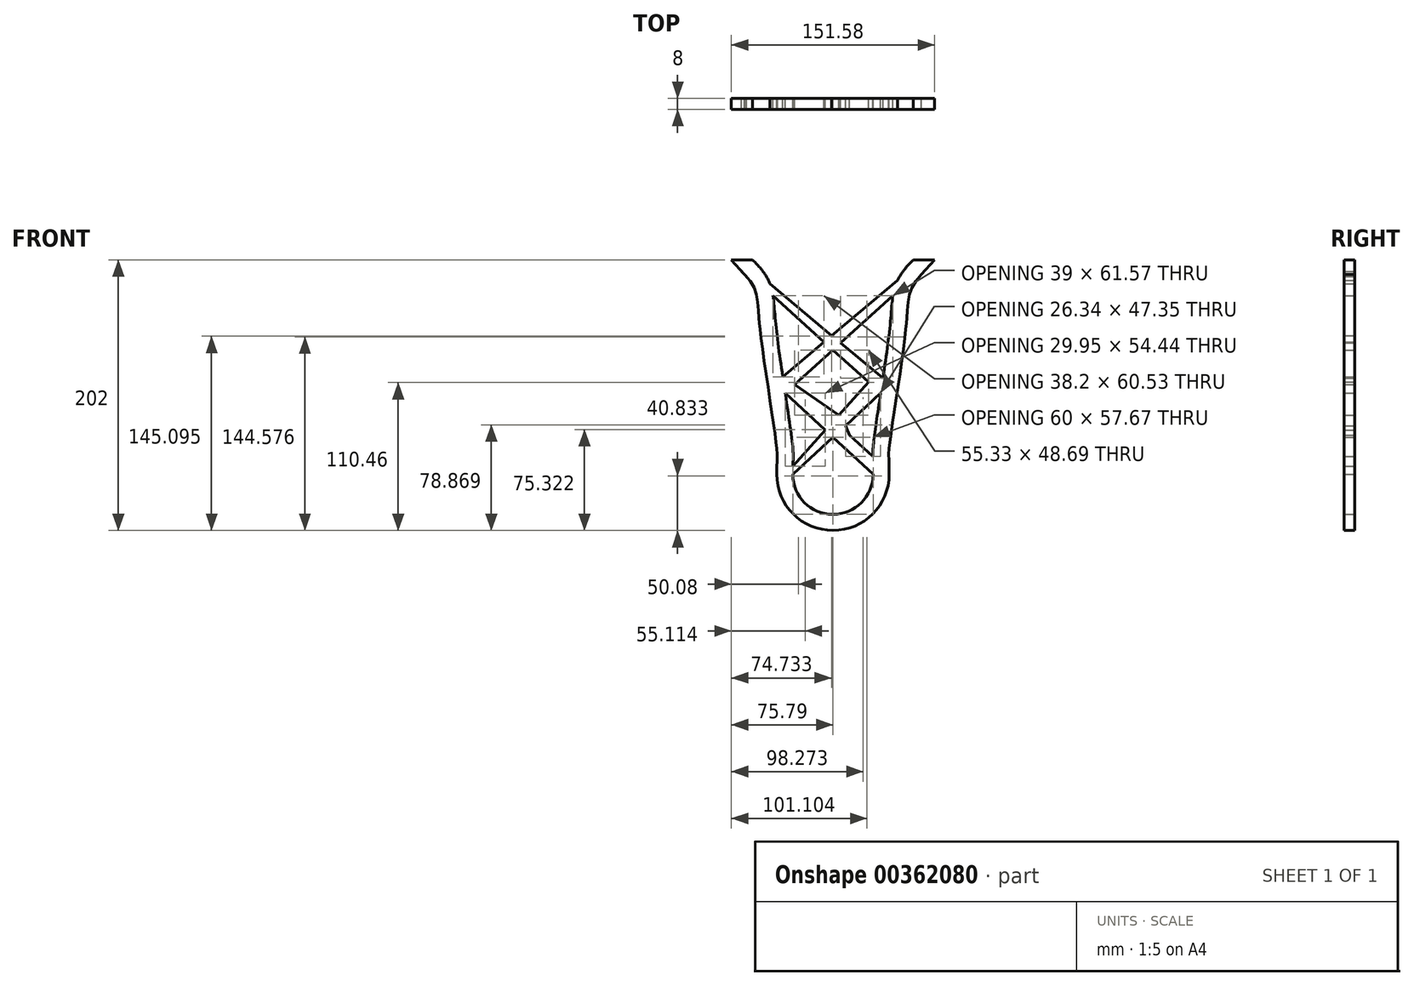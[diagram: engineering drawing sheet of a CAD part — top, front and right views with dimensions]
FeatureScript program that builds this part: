
annotation { "Feature Type Name" : "Feature", "Feature Type Description" : "" }
export const myFeature = defineFeature(function(context is Context, id is Id, definition is map)
    precondition{}
    {
        {
            var Q0;
            Q0=qCreatedBy(makeId("Front.planeOp"),FACE);
            var sketch = newSketch(context, id + "F0", { "sketchPlane" : qUnion([Q0])});
            skArc(sketch, "E0", {"start": v(-30, 0) * mm, "mid": v(0, -30) * mm, "end": v(30, 0) * mm});
            skLineSegment(sketch, "E1", {"start": v(30, 0) * mm, "end": v(0, 0) * mm, "construction": true});
            skLineSegment(sketch, "E2", {"start": v(-30, 0) * mm, "end": v(0, 0) * mm, "construction": true});
            skFitSpline(sketch, "E3", {"points": [v(30, 0) * mm, v(30, 20) * mm, v(43, 115) * mm, v(60, 160) * mm], "startDerivative": vector(0, 145.41) * mm, "endDerivative": vector(149.4, 141.79) * mm});
            skLineSegment(sketch, "E4", {"start": v(0, 0) * mm, "end": v(0, 155.66) * mm, "construction": true});
            skLineSegment(sketch, "E5", {"start": v(30, 20) * mm, "end": v(0, 20) * mm, "construction": true});
            skLineSegment(sketch, "E6", {"start": v(43, 115) * mm, "end": v(0, 115) * mm, "construction": true});
            skLineSegment(sketch, "E7", {"start": v(60, 160) * mm, "end": v(0, 160) * mm, "construction": true});
            skFitSpline(sketch, "E8.0", {"points": [v(42, 0) * mm, v(42, 1.6) * mm, v(41.97, 4.43) * mm, v(41.86, 7.8) * mm, v(41.74, 10.43) * mm, v(41.67, 12.52) * mm, v(41.67, 14.41) * mm, v(41.74, 16.25) * mm, v(41.88, 18.1) * mm, v(42.02, 19.7) * mm, v(42.22, 21.59) * mm, v(42.54, 24.4) * mm, v(43.06, 28.42) * mm, v(43.82, 33.94) * mm, v(44.7, 40.04) * mm, v(45.68, 46.6) * mm, v(46.73, 53.55) * mm, v(48.19, 63.16) * mm, v(49.68, 73.11) * mm, v(51.12, 83.03) * mm, v(52.14, 90.35) * mm, v(53.09, 97.46) * mm, v(53.8, 103.15) * mm, v(54.3, 107.5) * mm, v(54.58, 110.14) * mm, v(54.79, 112.19) * mm, v(54.93, 113.7) * mm, v(55.07, 115.17) * mm, v(55.23, 117.08) * mm, v(55.42, 119.34) * mm, v(55.7, 122.74) * mm, v(56.02, 126.54) * mm, v(56.47, 130.44) * mm, v(57.04, 133.72) * mm, v(57.77, 136.53) * mm, v(58.73, 139.07) * mm, v(60.04, 141.6) * mm, v(61.9, 144.4) * mm, v(64.52, 147.58) * mm, v(66.9, 150) * mm, v(68.26, 151.3) * mm]});
            skArc(sketch, "E9.0", {"start": v(-42, 0) * mm, "mid": v(0, -42) * mm, "end": v(42, 0) * mm});
            skLineSegment(sketch, "E10", {"start": v(60, 160) * mm, "end": v(75.8, 160) * mm});
            skLineSegment(sketch, "E11", {"start": v(64.53, 147.49) * mm, "end": v(75.8, 160) * mm});
            skLineSegment(sketch, "E12.MirrorCS", {"start": v(-60, 160) * mm, "end": v(-75.8, 160) * mm});
            skLineSegment(sketch, "E13.MirrorCS", {"start": v(-64.53, 147.49) * mm, "end": v(-75.8, 160) * mm});
            skFitSpline(sketch, "E14.MirrorCS", {"points": [v(-30, 0) * mm, v(-30, 20) * mm, v(-43, 115) * mm, v(-60, 160) * mm], "startDerivative": vector(0, 145.41) * mm, "endDerivative": vector(-149.4, 141.79) * mm});
            skFitSpline(sketch, "E15.0", {"points": [v(-42, 0) * mm, v(-42, 1.6) * mm, v(-41.97, 4.43) * mm, v(-41.86, 7.8) * mm, v(-41.74, 10.43) * mm, v(-41.67, 12.52) * mm, v(-41.67, 14.41) * mm, v(-41.74, 16.25) * mm, v(-41.88, 18.1) * mm, v(-42.02, 19.7) * mm, v(-42.22, 21.59) * mm, v(-42.54, 24.4) * mm, v(-43.06, 28.42) * mm, v(-43.82, 33.94) * mm, v(-44.7, 40.04) * mm, v(-45.68, 46.6) * mm, v(-46.73, 53.55) * mm, v(-48.19, 63.16) * mm, v(-49.68, 73.11) * mm, v(-51.12, 83.03) * mm, v(-52.14, 90.35) * mm, v(-53.09, 97.46) * mm, v(-53.8, 103.15) * mm, v(-54.3, 107.5) * mm, v(-54.58, 110.14) * mm, v(-54.79, 112.19) * mm, v(-54.93, 113.7) * mm, v(-55.07, 115.17) * mm, v(-55.23, 117.08) * mm, v(-55.42, 119.34) * mm, v(-55.7, 122.74) * mm, v(-56.02, 126.54) * mm, v(-56.47, 130.44) * mm, v(-57.04, 133.72) * mm, v(-57.77, 136.53) * mm, v(-58.73, 139.07) * mm, v(-60.04, 141.6) * mm, v(-61.9, 144.4) * mm, v(-64.52, 147.58) * mm, v(-66.9, 150) * mm, v(-68.26, 151.3) * mm]});
            skLineSegment(sketch, "E16", {"start": v(30, 0) * mm, "end": v(0, 27.67) * mm});
            skLineSegment(sketch, "E17", {"start": v(-30, 0) * mm, "end": v(0, 27.67) * mm});
            skLineSegment(sketch, "E18", {"start": v(26.6, 68.73) * mm, "end": v(0, 92.8) * mm});
            skLineSegment(sketch, "E19", {"start": v(-28.72, 66.81) * mm, "end": v(0, 92.8) * mm});
            skLineSegment(sketch, "E20", {"start": v(0, 60.54) * mm, "end": v(-35.65, 60.54) * mm, "construction": true});
            skLineSegment(sketch, "E21", {"start": v(0, 60.54) * mm, "end": v(35.65, 60.54) * mm, "construction": true});
            skLineSegment(sketch, "E22", {"start": v(29.67, 13.2) * mm, "end": v(12.26, 29.25) * mm});
            skLineSegment(sketch, "E23", {"start": v(-7.49, 30.94) * mm, "end": v(-29.9, 6.1) * mm});
            skLineSegment(sketch, "E24", {"start": v(-7.49, 30.94) * mm, "end": v(-5.7, 32.92) * mm});
            skLineSegment(sketch, "E25.trimOffspring", {"start": v(9.32, 36.26) * mm, "end": v(35.65, 60.54) * mm});
            skLineSegment(sketch, "E26.trimOffspring", {"start": v(4.4, 44.11) * mm, "end": v(-28.72, 66.81) * mm});
            skLineSegment(sketch, "E27.trimOffspring", {"start": v(4.4, 44.11) * mm, "end": v(26.6, 68.73) * mm});
            skLineSegment(sketch, "E28.trimOffspring", {"start": v(-5.7, 32.92) * mm, "end": v(-35.65, 60.54) * mm});
            skFitSpline(sketch, "E29.trimOffspring", {"points": [v(30, 0) * mm, v(30, 20) * mm, v(43, 115) * mm, v(60, 160) * mm], "startDerivative": vector(0, 145.41) * mm, "endDerivative": vector(149.4, 141.79) * mm});
            skLineSegment(sketch, "E30", {"start": v(12.26, 29.25) * mm, "end": v(9.32, 36.26) * mm});
            skLineSegment(sketch, "E31", {"start": v(-47.1, 142.17) * mm, "end": v(-0.85, 103.63) * mm});
            skLineSegment(sketch, "E32", {"start": v(-37.5, 72.83) * mm, "end": v(-6.6, 98.79) * mm});
            skPoint(sketch, "E33.start.orphan", {"position": v(0, 134) * mm});
            skLineSegment(sketch, "E34.trimOffspring", {"start": v(5.82, 98.07) * mm, "end": v(37.34, 71.8) * mm});
            skLineSegment(sketch, "E35.trimOffspring", {"start": v(-0.85, 103.63) * mm, "end": v(48.27, 144.9) * mm});
            skLineSegment(sketch, "E36.trimOffspring", {"start": v(-6.6, 98.79) * mm, "end": v(-44.81, 133.36) * mm});
            skLineSegment(sketch, "E37.trimOffspring", {"start": v(5.82, 98.07) * mm, "end": v(44.81, 133.36) * mm});
            skLineSegment(sketch, "E38", {"start": v(-64.53, 147.49) * mm, "end": v(-68.26, 151.3) * mm});
            skSolve(sketch);
        }
        {
            var Q0;
            Q0 = qSketchRegion(id + "F0", true);
            extrude(context, id + "F1", {"entities" : qUnion([Q0]), "depth" : 8 * mm});
        }
    });
